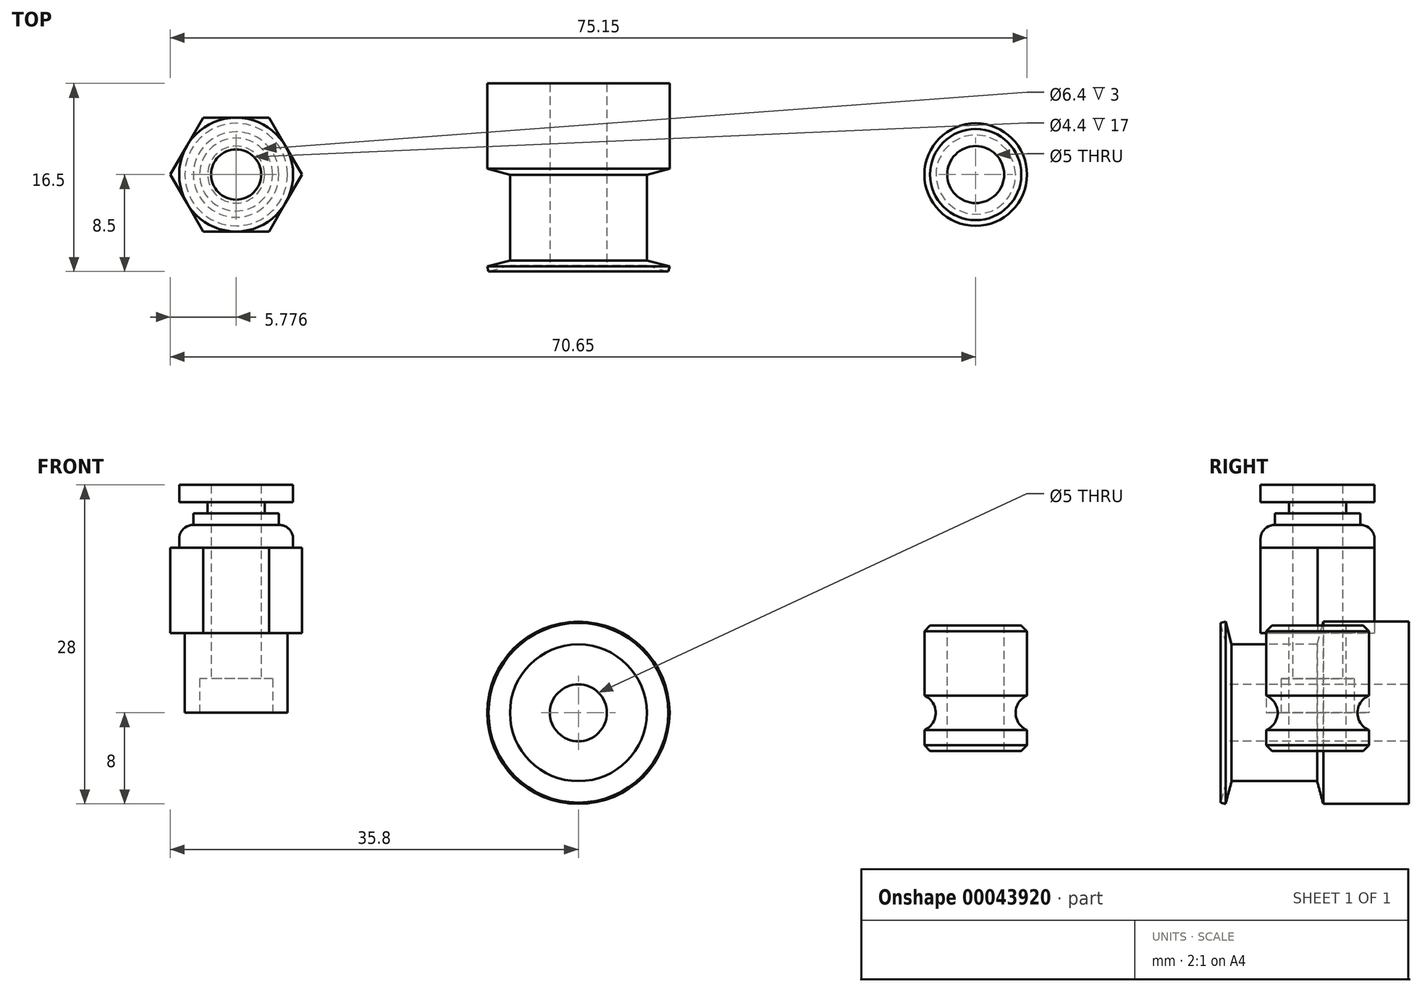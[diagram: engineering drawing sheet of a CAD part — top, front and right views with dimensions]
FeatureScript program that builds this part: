
annotation { "Feature Type Name" : "Feature", "Feature Type Description" : "" }
export const myFeature = defineFeature(function(context is Context, id is Id, definition is map)
    precondition{}
    {
        {
            var Q0;
            Q0=qCreatedBy(makeId("Right.planeOp"),FACE);
            var sketch = newSketch(context, id + "F0", { "sketchPlane" : qUnion([Q0])});
            skLineSegment(sketch, "E0", {"start": v(-20.69, 0) * mm, "end": v(25.26, 0) * mm, "construction": true});
            skLineSegment(sketch, "E1", {"start": v(-8, 0) * mm, "end": v(-8, 6) * mm});
            skLineSegment(sketch, "E2", {"start": v(-8, 6) * mm, "end": v(-8.5, 7.88) * mm});
            skLineSegment(sketch, "E3", {"start": v(-8.5, 7.88) * mm, "end": v(-8.07, 8) * mm});
            skLineSegment(sketch, "E4", {"start": v(-8.07, 8) * mm, "end": v(-7.54, 6) * mm});
            skLineSegment(sketch, "E5", {"start": v(-7.54, 6) * mm, "end": v(-0.04, 6) * mm});
            skLineSegment(sketch, "E6", {"start": v(-0.04, 6) * mm, "end": v(0.5, 8) * mm});
            skLineSegment(sketch, "E7", {"start": v(0.5, 8) * mm, "end": v(8, 8) * mm});
            skLineSegment(sketch, "E8", {"start": v(8, 8) * mm, "end": v(8, 0) * mm});
            skLineSegment(sketch, "E9", {"start": v(8, 0) * mm, "end": v(-8, 0) * mm});
            skLineSegment(sketch, "E10", {"start": v(-8, 2.5) * mm, "end": v(8, 2.5) * mm});
            skSolve(sketch);
        }
        {
            var Q0;
            {var subQ3=sQuery(id+"F0.wireOp",EDGE,"E2");Q0=makeQuery(id+"F0.imprint","IMPRINT",FACE,{"disambiguationData":[TD([[makeQuery(id+"F0.imprint","IMPRINT",EDGE,{"derivedFrom":subQ3}),-1.0]])]});}
            var Q1;
            Q1=sQuery(id+"F0.wireOp",EDGE,"E0");
            revolve(context, id + "F1", {"entities" : qUnion([Q0]), "axis" : qUnion([Q1]), "revolveType" : RevolveType.FULL});
        }
        {
            var Q0;
            Q0=qCreatedBy(makeId("Top.planeOp"),FACE);
            var sketch = newSketch(context, id + "F2", { "sketchPlane" : qUnion([Q0])});
            skCircle(sketch, "E11", {"center": v(-30.02, 0) * mm, "radius": 2.2 * mm});
            skCircle(sketch, "E12", {"center": v(-30.02, 0) * mm, "radius": 3.2 * mm});
            skCircle(sketch, "E13", {"center": v(-30.02, 0) * mm, "radius": 4.5 * mm});
            skSolve(sketch);
        }
        {
            var Q0;
            Q0=makeQuery(id+"F2.imprint","IMPRINT",FACE,{"disambiguationData":[TD([[makeQuery(id+"F2.imprint","IMPRINT",EDGE,{"derivedFrom":sQuery(id+"F2.wireOp",EDGE,"E12")}),-1.0]])]});
            extrude(context, id + "F3", {"entities" : qUnion([Q0]), "depth" : 3 * mm});
        }
        {
            var Q0;
            Q0=makeQuery(id+"F2.imprint","IMPRINT",FACE,{"disambiguationData":[TD([[makeQuery(id+"F2.imprint","IMPRINT",EDGE,{"derivedFrom":sQuery(id+"F2.wireOp",EDGE,"E11")}),-1.0]])]});
            extrude(context, id + "F4", {"entities" : qUnion([Q0]), "depth" : 7 * mm, "hasSecondDirection" : true, "secondDirectionOppositeDirection" : false, "secondDirectionDepth" : 3 * mm});
        }
        {
            var Q0;
            Q0=makeQuery(id+"F3.opExtrude","CAP_FACE",FACE,{"disambiguationData":[OSD([sQuery(id+"F2.wireOp",EDGE,"E12"),sQuery(id+"F2.wireOp",EDGE,"E13")])],"isStart":false});
            var Q1;
            Q1=makeQuery(id+"F4.opExtrude","CAP_FACE",FACE,{"disambiguationData":[OSD([sQuery(id+"F2.wireOp",EDGE,"E11"),sQuery(id+"F2.wireOp",EDGE,"E12")])],"isStart":false});
            extrude(context, id + "F5", {"entities" : qUnion([Q0]), "operationType" : NewBodyOperationType.ADD, "endBound" : BoundingType.UP_TO_SURFACE, "endBoundEntityFace" : qUnion([Q1]), "depth" : 25 * mm});
        }
        {
            var Q0;
            {var subQ0=sQuery(id+"F2.wireOp",EDGE,"E12");Q0=makeQuery(id+"F5.boolean.opBoolean","MERGE",FACE,{"derivedFrom":[makeQuery(id+"F4.opExtrude","CAP_FACE",FACE,{"disambiguationData":[OSD([sQuery(id+"F2.wireOp",EDGE,"E11"),subQ0])],"isStart":false}),makeQuery(id+"F5.opExtrude","CAP_FACE",FACE,{"disambiguationData":[OSD([subQ0,sQuery(id+"F2.wireOp",EDGE,"E13")])],"isStart":false})]});}
            var sketch = newSketch(context, id + "F6", { "sketchPlane" : qUnion([Q0])});
            skCircle(sketch, "E14.cCircle", {"center": v(-30.02, 0) * mm, "radius": 5 * mm, "construction": true});
            skLineSegment(sketch, "E14.0", {"start": v(-32.91, 5) * mm, "end": v(-27.14, 5) * mm});
            skLineSegment(sketch, "E14.1", {"start": v(-27.14, 5) * mm, "end": v(-24.25, 0) * mm});
            skLineSegment(sketch, "E14.2", {"start": v(-24.25, 0) * mm, "end": v(-27.14, -5) * mm});
            skLineSegment(sketch, "E14.3", {"start": v(-27.14, -5) * mm, "end": v(-32.91, -5) * mm});
            skLineSegment(sketch, "E14.4", {"start": v(-32.91, -5) * mm, "end": v(-35.8, 0) * mm});
            skLineSegment(sketch, "E14.5", {"start": v(-35.8, 0) * mm, "end": v(-32.91, 5) * mm});
            skPoint(sketch, "E14.0.midPoint", {"position": v(-30.02, 5) * mm});
            skSolve(sketch);
        }
        {
            var Q0;
            Q0=makeQuery(id+"F6.imprint","IMPRINT",FACE,{"disambiguationData":[TD([[makeQuery(id+"F6.imprint","IMPRINT",EDGE,{"derivedFrom":makeQuery(id+"F4.opExtrude","CAP_EDGE",EDGE,{"disambiguationData":[OSD([sQuery(id+"F2.wireOp",EDGE,"E11")])],"isStart":false})}),-1.0]])]});
            var Q1;
            Q1=makeQuery(id+"F6.imprint","IMPRINT",FACE,{"disambiguationData":[TD([[makeQuery(id+"F6.imprint","IMPRINT",EDGE,{"derivedFrom":sQuery(id+"F6.wireOp",EDGE,"E14.0")}),-1.0]])]});
            extrude(context, id + "F7", {"entities" : qUnion([Q0, Q1]), "operationType" : NewBodyOperationType.ADD, "depth" : 7.5 * mm});
        }
        {
            var Q0;
            Q0=makeQuery(id+"F7.opExtrude","CAP_FACE",FACE,{"disambiguationData":[OSD([sQuery(id+"F2.wireOp",EDGE,"E11"),sQuery(id+"F6.wireOp",EDGE,"E14.0"),sQuery(id+"F6.wireOp",EDGE,"E14.1"),sQuery(id+"F6.wireOp",EDGE,"E14.2"),sQuery(id+"F6.wireOp",EDGE,"E14.3"),sQuery(id+"F6.wireOp",EDGE,"E14.4"),sQuery(id+"F6.wireOp",EDGE,"E14.5")])],"isStart":false});
            var sketch = newSketch(context, id + "F8", { "sketchPlane" : qUnion([Q0])});
            skCircle(sketch, "E15", {"center": v(-30.02, 0) * mm, "radius": 5 * mm});
            skSolve(sketch);
        }
        {
            var Q0;
            Q0=qSketchRegion(id+"F8",true);
            extrude(context, id + "F9", {"entities" : qUnion([Q0]), "operationType" : NewBodyOperationType.ADD, "depth" : 2 * mm});
        }
        {
            var Q0;
            Q0=makeQuery(id+"F9.opExtrude","CAP_EDGE",EDGE,{"disambiguationData":[OSD([sQuery(id+"F8.wireOp",EDGE,"E15")])],"isStart":false});
            fillet(context, id + "F10", {"entities" : qUnion([Q0]), "radius" : 1.25 * mm, "tangentPropagation" : true, "allowEdgeOverflow" : false});
        }
        {
            var Q0;
            Q0=makeQuery(id+"F9.opExtrude","CAP_FACE",FACE,{"disambiguationData":[OSD([sQuery(id+"F8.wireOp",EDGE,"E15")])],"isStart":false});
            extrude(context, id + "F11", {"entities" : qUnion([Q0]), "operationType" : NewBodyOperationType.ADD, "depth" : 1 * mm});
        }
        {
            var Q0;
            Q0=makeQuery(id+"F11.opExtrude","CAP_FACE",FACE,{"disambiguationData":[OSD([sQuery(id+"F8.wireOp",EDGE,"E15")])],"isStart":false});
            var sketch = newSketch(context, id + "F12", { "sketchPlane" : qUnion([Q0])});
            skCircle(sketch, "E16", {"center": v(-30.02, 0) * mm, "radius": 2.5 * mm});
            skSolve(sketch);
        }
        {
            var Q0;
            Q0=makeQuery(id+"F12.imprint","IMPRINT",FACE,{"disambiguationData":[TD([[makeQuery(id+"F12.imprint","IMPRINT",EDGE,{"derivedFrom":sQuery(id+"F12.wireOp",EDGE,"E16")}),1.0]])]});
            extrude(context, id + "F13", {"entities" : qUnion([Q0]), "operationType" : NewBodyOperationType.ADD, "depth" : 1 * mm});
        }
        {
            var Q0;
            Q0=makeQuery(id+"F13.opExtrude","CAP_FACE",FACE,{"disambiguationData":[OSD([sQuery(id+"F12.wireOp",EDGE,"E16")])],"isStart":false});
            var sketch = newSketch(context, id + "F14", { "sketchPlane" : qUnion([Q0])});
            skCircle(sketch, "E17", {"center": v(-30.02, 0) * mm, "radius": 5 * mm});
            skSolve(sketch);
        }
        {
            var Q0;
            Q0=makeQuery(id+"F14.imprint","IMPRINT",FACE,{"disambiguationData":[TD([[makeQuery(id+"F14.imprint","IMPRINT",EDGE,{"derivedFrom":sQuery(id+"F14.wireOp",EDGE,"E17")}),1.0]])]});
            var Q1;
            Q1=makeQuery(id+"F14.imprint","IMPRINT",FACE,{"disambiguationData":[TD([[makeQuery(id+"F14.imprint","IMPRINT",EDGE,{"derivedFrom":makeQuery(id+"F13.opExtrude","CAP_EDGE",EDGE,{"disambiguationData":[OSD([sQuery(id+"F12.wireOp",EDGE,"E16")])],"isStart":false})}),1.0]])]});
            extrude(context, id + "F15", {"entities" : qUnion([Q0, Q1]), "operationType" : NewBodyOperationType.ADD, "depth" : 1.5 * mm});
        }
        {
            var Q0;
            Q0=makeQuery(id+"F2.imprint","IMPRINT",FACE,{"disambiguationData":[TD([[makeQuery(id+"F2.imprint","IMPRINT",EDGE,{"derivedFrom":sQuery(id+"F2.wireOp",EDGE,"E11")}),1.0]])]});
            extrude(context, id + "F16", {"entities" : qUnion([Q0]), "operationType" : NewBodyOperationType.REMOVE, "endBound" : BoundingType.THROUGH_ALL, "depth" : 25 * mm});
        }
        {
            var Q0;
            Q0=qCreatedBy(makeId("Front.planeOp"),FACE);
            var sketch = newSketch(context, id + "F17", { "sketchPlane" : qUnion([Q0])});
            skLineSegment(sketch, "E18", {"start": v(34.85, 8.73) * mm, "end": v(34.85, -5.57) * mm, "construction": true});
            skLineSegment(sketch, "E19", {"start": v(34.85, 7.65) * mm, "end": v(38.85, 7.65) * mm});
            skLineSegment(sketch, "E20", {"start": v(38.85, 7.65) * mm, "end": v(39.35, 7.15) * mm});
            skLineSegment(sketch, "E21", {"start": v(39.35, 7.15) * mm, "end": v(39.35, 1.52) * mm});
            skLineSegment(sketch, "E22", {"start": v(34.85, -3.35) * mm, "end": v(38.85, -3.35) * mm});
            skLineSegment(sketch, "E23", {"start": v(38.85, -3.35) * mm, "end": v(39.35, -2.85) * mm});
            skLineSegment(sketch, "E24", {"start": v(39.35, -2.85) * mm, "end": v(39.35, -1.52) * mm});
            skLineSegment(sketch, "E25", {"start": v(37.35, 7.65) * mm, "end": v(37.35, -3.35) * mm});
            skArc(sketch, "E26", {"start": v(39.35, 1.52) * mm, "mid": v(38.35, 0) * mm, "end": v(39.35, -1.52) * mm});
            skSolve(sketch);
        }
        {
            var Q0;
            {var subQ3=sQuery(id+"F17.wireOp",EDGE,"E20");Q0=makeQuery(id+"F17.imprint","IMPRINT",FACE,{"disambiguationData":[TD([[makeQuery(id+"F17.imprint","IMPRINT",EDGE,{"derivedFrom":subQ3}),-1.0]])]});}
            var Q1;
            Q1=sQuery(id+"F17.wireOp",EDGE,"E18");
            revolve(context, id + "F18", {"entities" : qUnion([Q0]), "axis" : qUnion([Q1]), "revolveType" : RevolveType.FULL});
        }
    });
